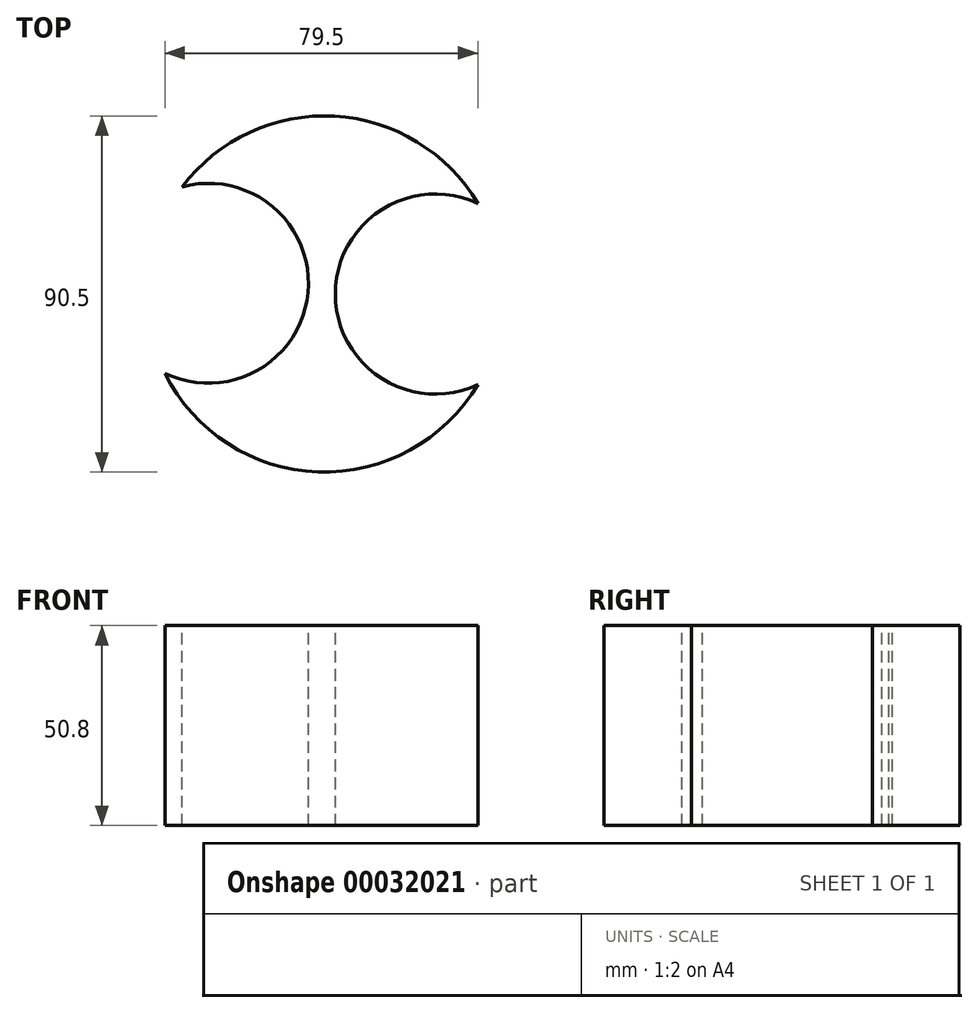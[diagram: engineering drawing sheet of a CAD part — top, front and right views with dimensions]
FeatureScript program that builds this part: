
annotation { "Feature Type Name" : "Feature", "Feature Type Description" : "" }
export const myFeature = defineFeature(function(context is Context, id is Id, definition is map)
    precondition{}
    {
        {
            var Q0;
            Q0=qCreatedBy(makeId("Top.planeOp"),FACE);
            var sketch = newSketch(context, id + "F0", { "sketchPlane" : qUnion([Q0])});
            skCircle(sketch, "E0", {"center": v(0, 0) * mm, "radius": 45.25 * mm});
            skSolve(sketch);
        }
        {
            var Q0;
            Q0=makeQuery(id+"F0.imprint","IMPRINT",FACE,{"disambiguationData":[TD([[makeQuery(id+"F0.imprint","IMPRINT",EDGE,{"derivedFrom":sQuery(id+"F0.wireOp",EDGE,"E0")}),1.0]])]});
            extrude(context, id + "F1", {"entities" : qUnion([Q0]), "depth" : 25.4 * mm});
        }
        {
            var Q0;
            Q0=makeQuery(id+"F1.opExtrude","CAP_FACE",FACE,{"disambiguationData":[OSD([sQuery(id+"F0.wireOp",EDGE,"E0")])],"isStart":false});
            extrude(context, id + "F2", {"entities" : qUnion([Q0]), "operationType" : NewBodyOperationType.ADD, "depth" : 25.4 * mm});
        }
        {
            var Q0;
            Q0=makeQuery(id+"F2.opExtrude","CAP_FACE",FACE,{"disambiguationData":[OSD([sQuery(id+"F0.wireOp",EDGE,"E0")])],"isStart":false});
            var sketch = newSketch(context, id + "F3", { "sketchPlane" : qUnion([Q0])});
            skCircle(sketch, "E1", {"center": v(-29.47, 2.73) * mm, "radius": 7.6 * mm});
            skCircle(sketch, "E2", {"center": v(28.16, 0) * mm, "radius": 7.73 * mm});
            skSolve(sketch);
        }
        {
            var Q0;
            Q0=sQuery(id+"F3.wireOp",VERTEX,"E1.center");
            var Q1;
            Q1=sQuery(id+"F3.wireOp",VERTEX,"E2.center");
            var Q2;
            Q2=makeQuery(id+"F1.opExtrude","SWEPT_BODY",BODY,{"disambiguationData":[OSD([sQuery(id+"F0.wireOp",EDGE,"E0")])]});
            hole(context, id + "F4", {"style" : HoleStyle.SIMPLE, "holeDiameter" : 50.8 * mm, "endStyle" : HoleEndStyle.THROUGH, "locations" : qUnion([Q0, Q1]), "scope" : qUnion([Q2])});
        }
    });
